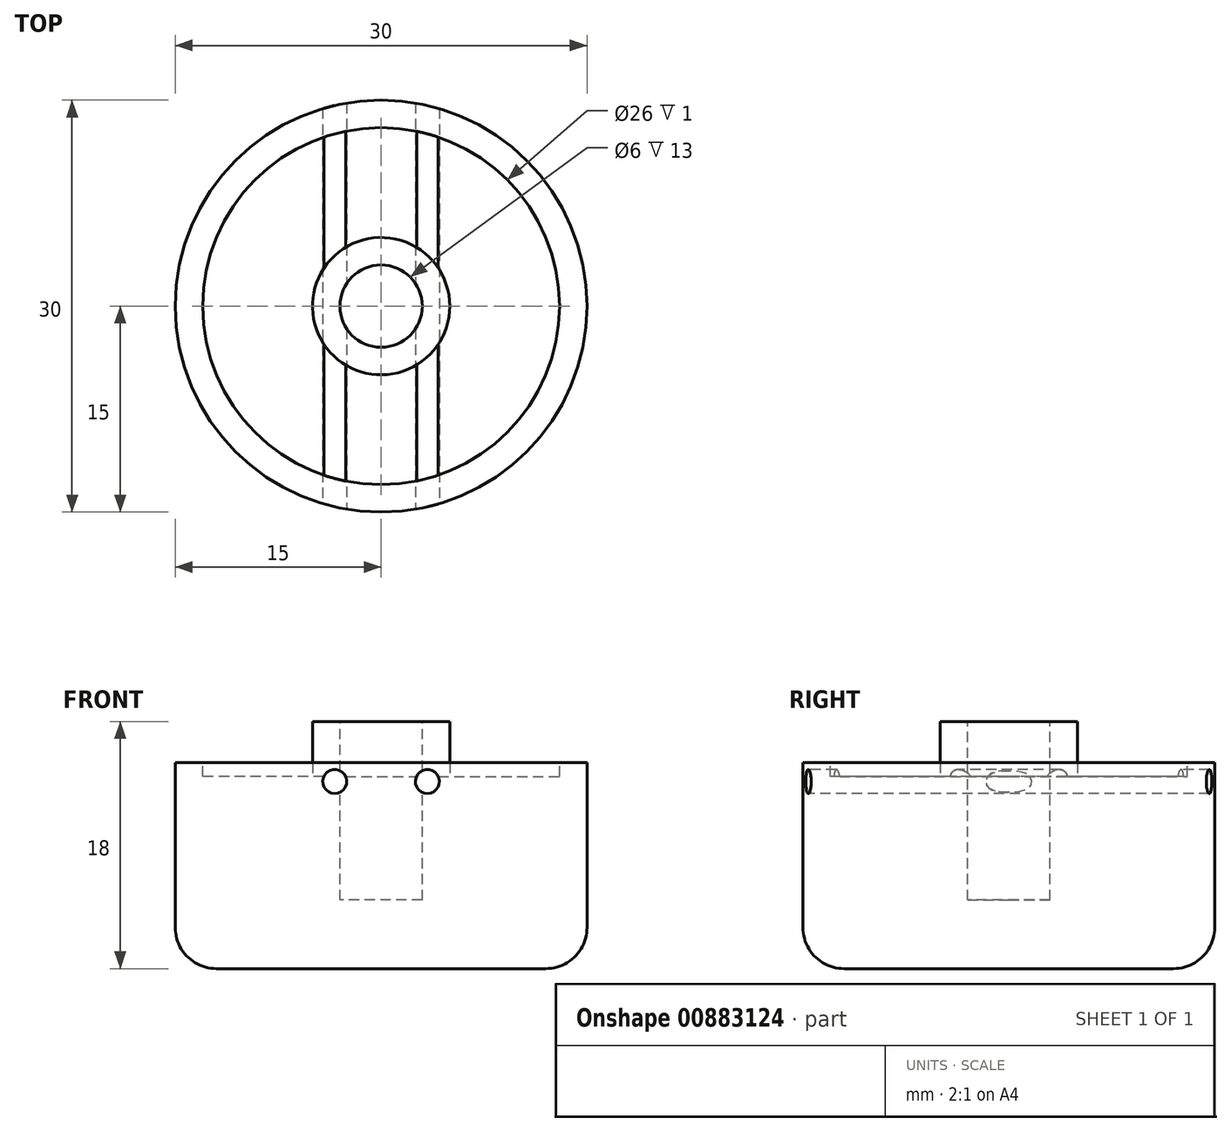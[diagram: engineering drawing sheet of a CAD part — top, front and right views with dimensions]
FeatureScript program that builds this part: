
annotation { "Feature Type Name" : "Feature", "Feature Type Description" : "" }
export const myFeature = defineFeature(function(context is Context, id is Id, definition is map)
    precondition{}
    {
        {
            var Q0;
            Q0=qCreatedBy(makeId("Top.planeOp"),FACE);
            var sketch = newSketch(context, id + "F0", { "sketchPlane" : qUnion([Q0])});
            skCircle(sketch, "E0", {"center": v(0, 0) * mm, "radius": 15 * mm});
            skSolve(sketch);
        }
        {
            var Q0;
            Q0 = qSketchRegion(id + "F0", true);
            extrude(context, id + "F1", {"entities" : qUnion([Q0]), "depth" : 15 * mm, "offsetDistance" : 25 * mm});
        }
        {
            var Q0;
            Q0=makeQuery(id+"F1.opExtrude","CAP_FACE",FACE,{"disambiguationData":[OSD([sQuery(id+"F0.wireOp",EDGE,"E0")])],"isStart":false});
            var sketch = newSketch(context, id + "F2", { "sketchPlane" : qUnion([Q0])});
            skCircle(sketch, "E1", {"center": v(0, 0) * mm, "radius": 13 * mm});
            skSolve(sketch);
        }
        {
            var Q0;
            Q0 = qSketchRegion(id + "F2", true);
            extrude(context, id + "F3", {"entities" : qUnion([Q0]), "operationType" : NewBodyOperationType.REMOVE, "oppositeDirection" : true, "depth" : 1 * mm, "offsetDistance" : 25 * mm});
        }
        {
            var Q0;
            Q0=makeQuery(id+"F3.boolean.opBoolean","COPY",FACE,{"derivedFrom":makeQuery(id+"F3.opExtrude","CAP_FACE",FACE,{"disambiguationData":[OSD([sQuery(id+"F2.wireOp",EDGE,"E1")])],"isStart":false})});
            var sketch = newSketch(context, id + "F4", { "sketchPlane" : qUnion([Q0])});
            skCircle(sketch, "E2", {"center": v(0, 0) * mm, "radius": 5 * mm});
            skSolve(sketch);
        }
        {
            var Q0;
            Q0 = qSketchRegion(id + "F4", true);
            extrude(context, id + "F5", {"entities" : qUnion([Q0]), "operationType" : NewBodyOperationType.ADD, "depth" : 4 * mm, "offsetDistance" : 25 * mm});
        }
        {
            var Q0;
            Q0=makeQuery(id+"F5.opExtrude","CAP_FACE",FACE,{"disambiguationData":[OSD([sQuery(id+"F4.wireOp",EDGE,"E2")])],"isStart":false});
            var sketch = newSketch(context, id + "F6", { "sketchPlane" : qUnion([Q0])});
            skCircle(sketch, "E3", {"center": v(0, 0) * mm, "radius": 3 * mm});
            skSolve(sketch);
        }
        {
            var Q0;
            Q0 = qSketchRegion(id + "F6", true);
            extrude(context, id + "F7", {"entities" : qUnion([Q0]), "operationType" : NewBodyOperationType.REMOVE, "oppositeDirection" : true, "depth" : 13 * mm, "offsetDistance" : 25 * mm});
        }
        {
            var Q0;
            Q0=makeQuery(id+"F1.opExtrude","CAP_EDGE",EDGE,{"disambiguationData":[OSD([sQuery(id+"F0.wireOp",EDGE,"E0")])],"isStart":true});
            fillet(context, id + "F8", {"entities" : qUnion([Q0]), "radius" : 3 * mm, "tangentPropagation" : true, "allowEdgeOverflow" : false});
        }
        {
            var Q0;
            Q0=qCreatedBy(makeId("Front.planeOp"),FACE);
            var sketch = newSketch(context, id + "F9", { "sketchPlane" : qUnion([Q0])});
            skCircle(sketch, "E4", {"center": v(-3.37, 13.62) * mm, "radius": 0.88 * mm});
            skLineSegment(sketch, "E5.0", {"start": v(-3, 18) * mm, "end": v(3, 18) * mm, "construction": true});
            skLineSegment(sketch, "E6", {"start": v(-3, 18) * mm, "end": v(-3, 2) * mm, "construction": true});
            skLineSegment(sketch, "E7", {"start": v(0, 20.08) * mm, "end": v(0, 8.42) * mm, "construction": true});
            skCircle(sketch, "E8.MirrorC", {"center": v(3.37, 13.62) * mm, "radius": 0.88 * mm});
            skSolve(sketch);
        }
        {
            var Q0;
            Q0 = qSketchRegion(id + "F9", true);
            extrude(context, id + "F10", {"entities" : qUnion([Q0]), "operationType" : NewBodyOperationType.REMOVE, "endBound" : BoundingType.THROUGH_ALL, "oppositeDirection" : true, "depth" : 25 * mm, "offsetDistance" : 25 * mm, "hasSecondDirection" : true, "secondDirectionBound" : SecondDirectionBoundingType.THROUGH_ALL, "secondDirectionOppositeDirection" : false, "secondDirectionDepth" : 25 * mm});
        }
    });
